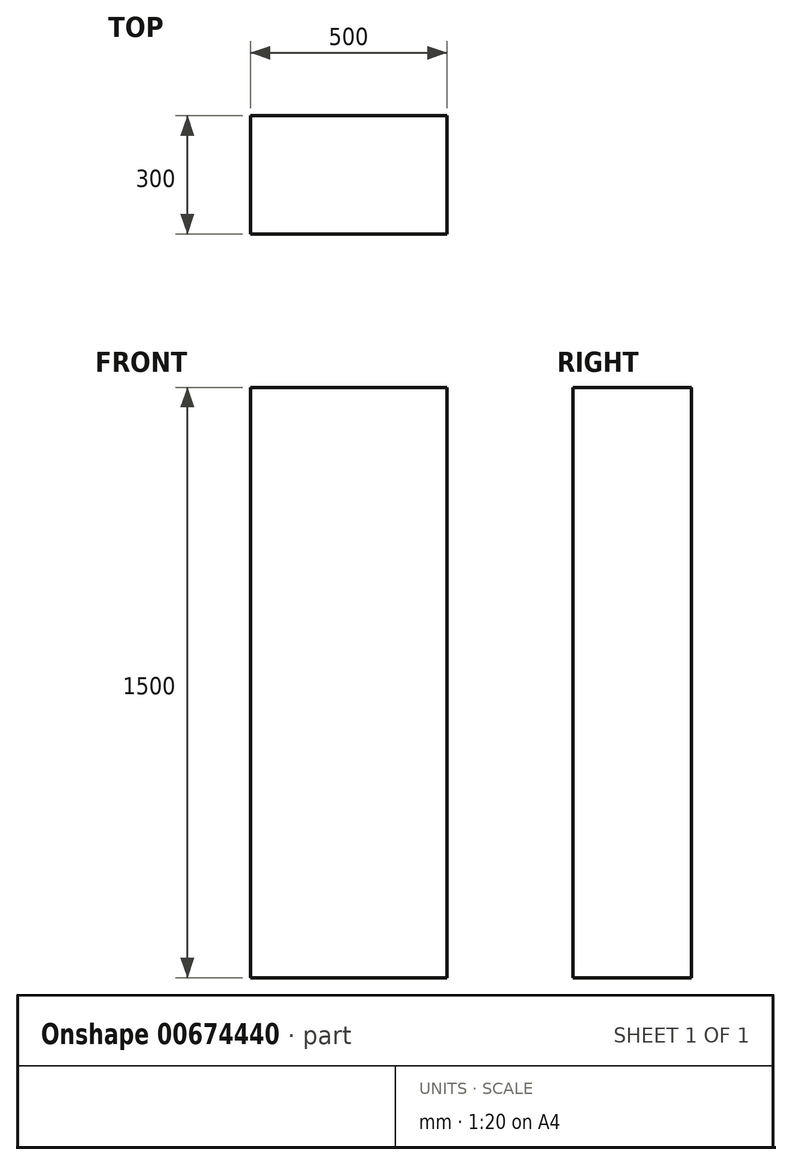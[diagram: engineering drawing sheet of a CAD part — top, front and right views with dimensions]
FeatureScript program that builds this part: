
annotation { "Feature Type Name" : "Feature", "Feature Type Description" : "" }
export const myFeature = defineFeature(function(context is Context, id is Id, definition is map)
    precondition{}
    {
        {
            var Q0;
            Q0=qCreatedBy(makeId("Top.planeOp"),FACE);
            var sketch = newSketch(context, id + "F0", { "sketchPlane" : qUnion([Q0])});
            skLineSegment(sketch, "E0.bottom", {"start": v(250, -150) * mm, "end": v(-250, -150) * mm});
            skLineSegment(sketch, "E0.top", {"start": v(250, 150) * mm, "end": v(-250, 150) * mm});
            skLineSegment(sketch, "E0.left", {"start": v(250, -150) * mm, "end": v(250, 150) * mm});
            skLineSegment(sketch, "E0.right", {"start": v(-250, -150) * mm, "end": v(-250, 150) * mm});
            skPoint(sketch, "E0.middle", {"position": v(0, 0) * mm});
            skSolve(sketch);
        }
        {
            var Q0;
            Q0 = qSketchRegion(id + "F0", true);
            extrude(context, id + "F1", {"entities" : qUnion([Q0]), "oppositeDirection" : true, "depth" : 1500 * mm, "offsetDistance" : 25 * mm});
        }
    });
